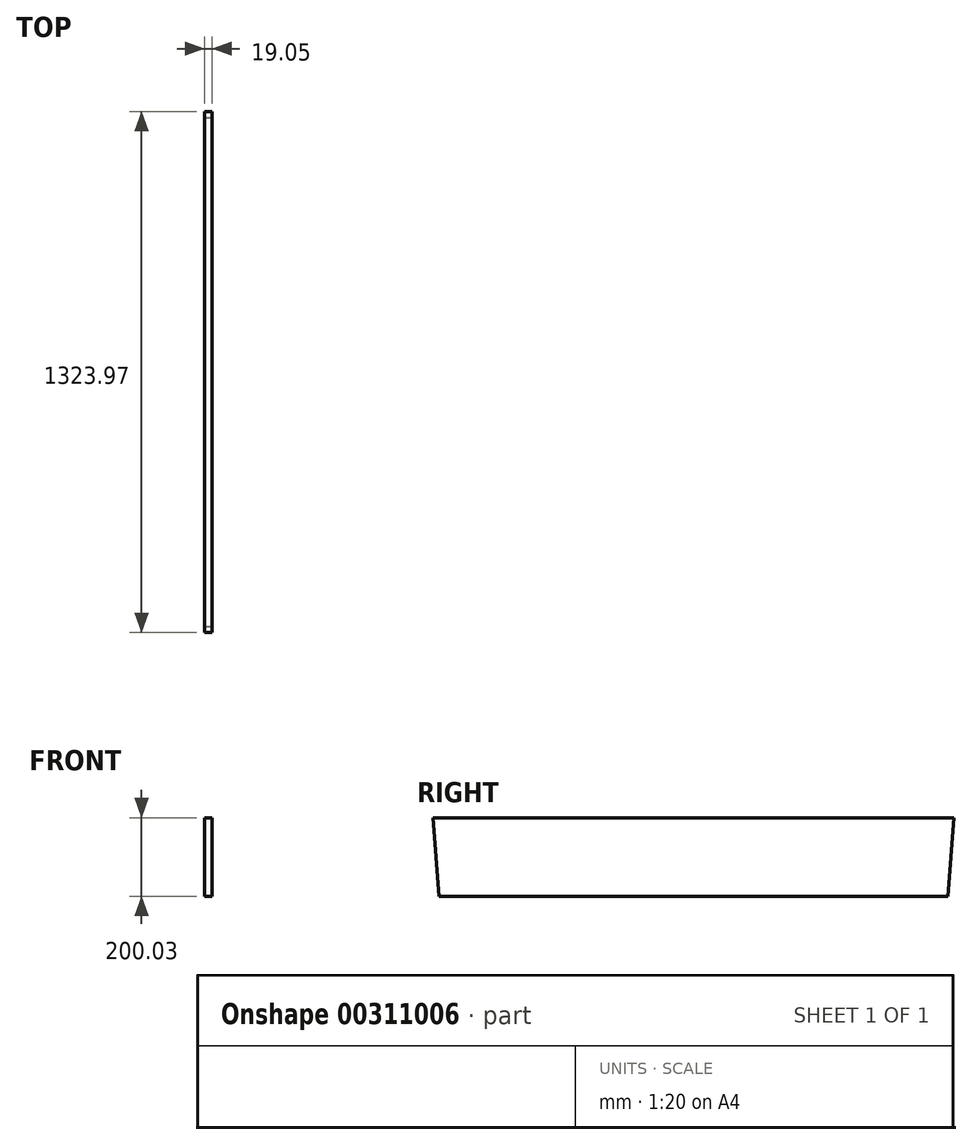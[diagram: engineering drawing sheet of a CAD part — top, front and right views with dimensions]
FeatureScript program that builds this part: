
annotation { "Feature Type Name" : "Feature", "Feature Type Description" : "" }
export const myFeature = defineFeature(function(context is Context, id is Id, definition is map)
    precondition{}
    {
        {
            var Q0;
            Q0=qCreatedBy(makeId("Right.planeOp"),FACE);
            var sketch = newSketch(context, id + "F0", { "sketchPlane" : qUnion([Q0])});
            skLineSegment(sketch, "E0", {"start": v(0, 0) * mm, "end": v(1323.97, 0) * mm});
            skLineSegment(sketch, "E1", {"start": v(1323.97, 0) * mm, "end": v(1308.1, -200.02) * mm});
            skLineSegment(sketch, "E2", {"start": v(1308.1, -200.02) * mm, "end": v(15.87, -200.02) * mm});
            skLineSegment(sketch, "E3", {"start": v(15.87, -200.03) * mm, "end": v(0, 0) * mm});
            skSolve(sketch);
        }
        {
            var Q0;
            Q0=makeQuery(id+"F0.imprint","IMPRINT",FACE,{"disambiguationData":[TD([[makeQuery(id+"F0.imprint","IMPRINT",EDGE,{"derivedFrom":sQuery(id+"F0.wireOp",EDGE,"E0")}),-1.0]])]});
            extrude(context, id + "F1", {"entities" : qUnion([Q0]), "oppositeDirection" : true, "depth" : 19.05 * mm});
        }
    });
